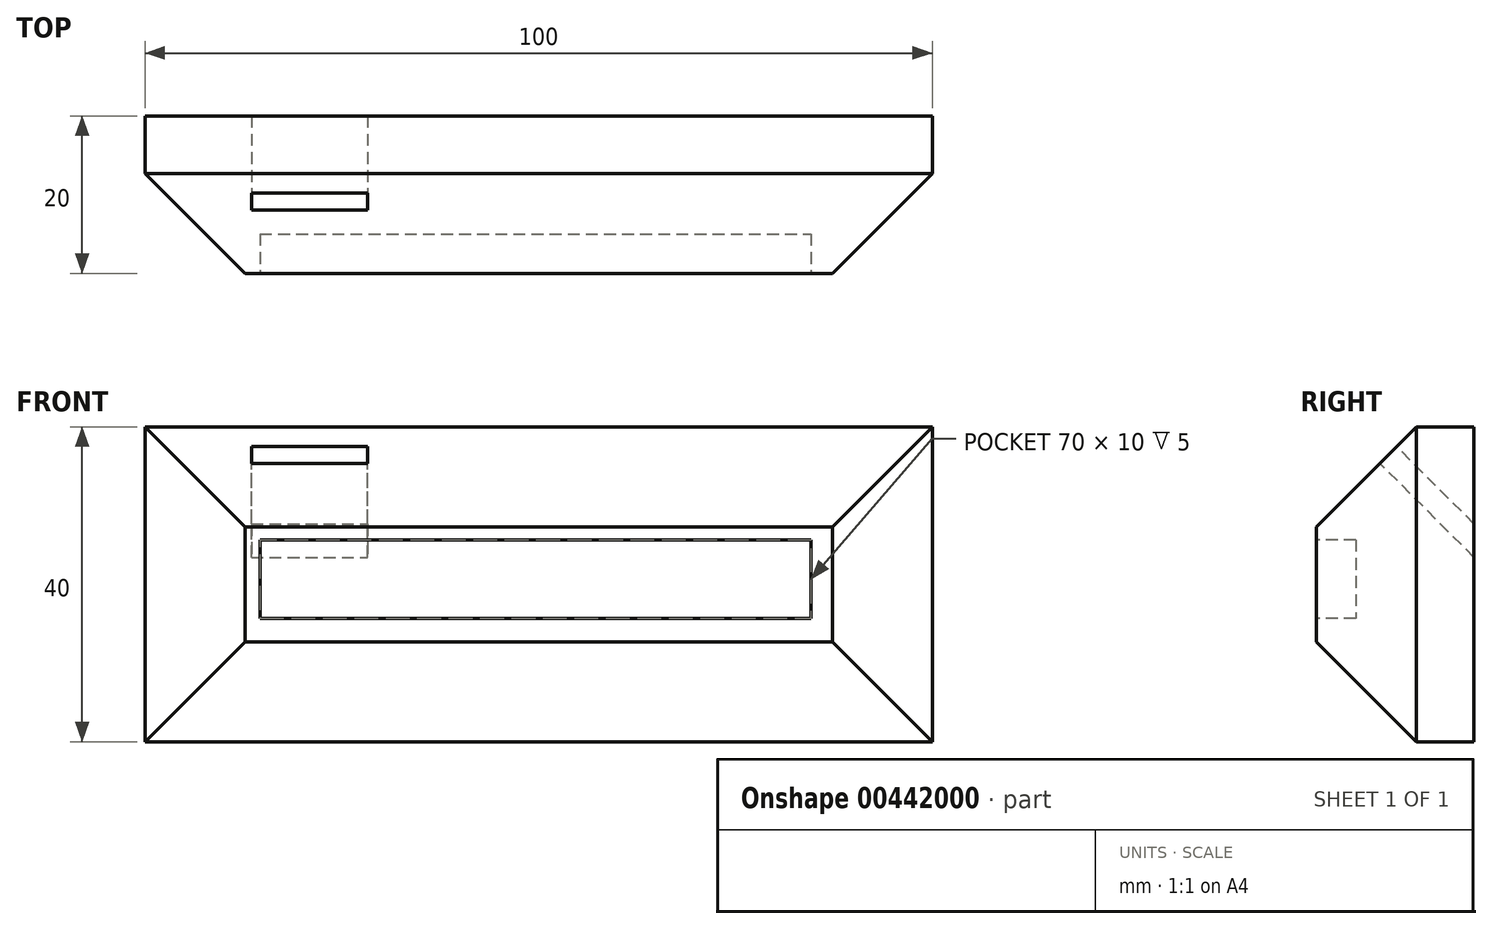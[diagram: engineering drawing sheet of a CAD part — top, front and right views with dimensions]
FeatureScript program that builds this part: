
annotation { "Feature Type Name" : "Feature", "Feature Type Description" : "" }
export const myFeature = defineFeature(function(context is Context, id is Id, definition is map)
    precondition{}
    {
        {
            var Q0;
            Q0=qCreatedBy(makeId("Front.planeOp"),FACE);
            var sketch = newSketch(context, id + "F0", { "sketchPlane" : qUnion([Q0])});
            skLineSegment(sketch, "E0.bottom", {"start": v(-70.02, -27.65) * mm, "end": v(29.98, -27.65) * mm});
            skLineSegment(sketch, "E0.top", {"start": v(-70.02, 12.35) * mm, "end": v(29.98, 12.35) * mm});
            skLineSegment(sketch, "E0.left", {"start": v(-70.02, -27.65) * mm, "end": v(-70.02, 12.35) * mm});
            skLineSegment(sketch, "E0.right", {"start": v(29.98, -27.65) * mm, "end": v(29.98, 12.35) * mm});
            skPoint(sketch, "E1.middle", {"position": v(0, 0) * mm});
            skSolve(sketch);
        }
        {
            var Q0;
            Q0=makeQuery(id+"F0.imprint","IMPRINT",FACE,{"disambiguationData":[TD([[makeQuery(id+"F0.imprint","IMPRINT",EDGE,{"derivedFrom":sQuery(id+"F0.wireOp",EDGE,"E0.bottom")}),1.0]])]});
            extrude(context, id + "F1", {"entities" : qUnion([Q0]), "depth" : 20 * mm, "offsetDistance" : 25 * mm});
        }
        {
            var Q0;
            Q0=makeQuery(id+"F1.opExtrude","CAP_EDGE",EDGE,{"disambiguationData":[OSD([sQuery(id+"F0.wireOp",EDGE,"E0.left")])],"isStart":false});
            var Q1;
            Q1=makeQuery(id+"F1.opExtrude","CAP_EDGE",EDGE,{"disambiguationData":[OSD([sQuery(id+"F0.wireOp",EDGE,"E0.right")])],"isStart":false});
            var Q2;
            Q2=makeQuery(id+"F1.opExtrude","CAP_EDGE",EDGE,{"disambiguationData":[OSD([sQuery(id+"F0.wireOp",EDGE,"E0.bottom")])],"isStart":false});
            var Q3;
            Q3=makeQuery(id+"F1.opExtrude","CAP_EDGE",EDGE,{"disambiguationData":[OSD([sQuery(id+"F0.wireOp",EDGE,"E0.top")])],"isStart":false});
            chamfer(context, id + "F2", {"entities" : qUnion([Q0, Q1, Q2, Q3]), "width" : 12.7 * mm, "tangentPropagation" : true});
        }
        {
            var Q0;
            Q0=makeQuery(id+"F2.opChamfer","BLEND_FACE",FACE,{"disambiguationData":[OSD([sQuery(id+"F0.wireOp",EDGE,"E0.top")])]});
            var sketch = newSketch(context, id + "F3", { "sketchPlane" : qUnion([Q0])});
            skLineSegment(sketch, "E2.bottom", {"start": v(-56.53, 0) * mm, "end": v(-41.75, 0) * mm});
            skLineSegment(sketch, "E2.top", {"start": v(-56.53, -3) * mm, "end": v(-41.75, -3) * mm});
            skLineSegment(sketch, "E2.left", {"start": v(-56.53, 0) * mm, "end": v(-56.53, -3) * mm});
            skLineSegment(sketch, "E2.right", {"start": v(-41.75, 0) * mm, "end": v(-41.75, -3) * mm});
            skSolve(sketch);
        }
        {
            var Q0;
            Q0=makeQuery(id+"F3.imprint","IMPRINT",FACE,{"disambiguationData":[TD([[makeQuery(id+"F3.imprint","IMPRINT",EDGE,{"derivedFrom":sQuery(id+"F3.wireOp",EDGE,"E2.bottom")}),-1.0]])]});
            extrude(context, id + "F4", {"entities" : qUnion([Q0]), "operationType" : NewBodyOperationType.REMOVE, "oppositeDirection" : true, "depth" : 25 * mm, "offsetDistance" : 25 * mm});
        }
        {
            var Q0;
            Q0=makeQuery(id+"F1.opExtrude","CAP_FACE",FACE,{"disambiguationData":[OSD([sQuery(id+"F0.wireOp",EDGE,"E0.bottom"),sQuery(id+"F0.wireOp",EDGE,"E0.top"),sQuery(id+"F0.wireOp",EDGE,"E0.left"),sQuery(id+"F0.wireOp",EDGE,"E0.right")])],"isStart":false});
            var sketch = newSketch(context, id + "F5", { "sketchPlane" : qUnion([Q0])});
            skLineSegment(sketch, "E3.bottom", {"start": v(-55.43, -2.02) * mm, "end": v(14.57, -2.02) * mm});
            skLineSegment(sketch, "E3.top", {"start": v(-55.43, -12.02) * mm, "end": v(14.57, -12.02) * mm});
            skLineSegment(sketch, "E3.left", {"start": v(-55.43, -2.02) * mm, "end": v(-55.43, -12.02) * mm});
            skLineSegment(sketch, "E3.right", {"start": v(14.57, -2.02) * mm, "end": v(14.57, -12.02) * mm});
            skSolve(sketch);
        }
        {
            var Q0;
            Q0=makeQuery(id+"F5.imprint","IMPRINT",FACE,{"disambiguationData":[TD([[makeQuery(id+"F5.imprint","IMPRINT",EDGE,{"derivedFrom":sQuery(id+"F5.wireOp",EDGE,"E3.bottom")}),-1.0]])]});
            extrude(context, id + "F6", {"entities" : qUnion([Q0]), "operationType" : NewBodyOperationType.REMOVE, "oppositeDirection" : true, "depth" : 5 * mm, "offsetDistance" : 25 * mm});
        }
    });
